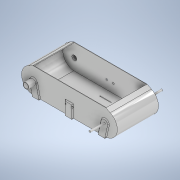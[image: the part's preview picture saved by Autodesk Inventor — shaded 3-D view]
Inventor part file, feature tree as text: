
AUTODESK INVENTOR PART (.ipt)
format: ipt  version: 2021 (Build 250183000, 183)  size: 548,352 bytes
history: native  units: mm
features: sketch x20, extrude x19, projected_geometry x8, fillet x3
ambient origin geometry x8: Origin, YZ Plane, XZ Plane, XY Plane, X Axis, Y Axis, Z Axis, Center Point
bodies: Solid1 (feature_tree)
feature tree (50):
  extrude  "Extrusion1"  Depth=26.0mm
  extrude  "Extrusion3"  Depth=8.0mm
  extrude  "Extrusion4"  Depth=182.8mm TaperAngle=0.0deg
  extrude  "Extrusion5"  Depth=35.0mm TaperAngle=0.0deg
  extrude  "Extrusion6"  Depth=10.0mm TaperAngle=0.0deg
  extrude  "Extrusion7"  Depth=10.0mm
  extrude  "Extrusion8"  Depth=10.0mm
  extrude  "Extrusion12"  Depth=3.0mm
  sketch  "Sketch15"  dims[d42=10.0mm d44=2.0mm]
  extrude  "Extrusion13"  Depth=3.0mm
  sketch  "Sketch17"  dims[d48=4.712389mm d49=3.0mm]
  extrude  "Extrusion14"  Depth=40.0mm
  extrude  "wzmocnienie ramy 1"  Depth=10.0mm
  extrude  "wzmocnienie ramy 2"  Depth=160.0mm
  extrude  "wzmocnienie ramy 3"  TaperAngle=0.0deg  [1 undecoded]
  fillet  "spaw 1"  Radius=10.0mm
  extrude  "wzmocnienie ramy 4"  Depth=4.0mm TaperAngle=0.0deg
  extrude  "wzmocnienie 5"  Depth=4.0mm TaperAngle=0.0deg
  extrude  "wzmocnienie ramy 6"  Depth=4.0mm
  fillet  "spaw 2"  Radius=4.0mm
  extrude  "wzmocnienie ramy 7"  Depth=4.0mm TaperAngle=0.0deg
  extrude  "wzmocnienie ramy 8"  Depth=4.0mm TaperAngle=0.0deg
  extrude  "wzmocnienie ramy 9"  Depth=3.9mm
  fillet  "spaw 3"  Radius=30.0mm
  sketch  "Sketch28"  dims[d85=4.0mm d86=0.0mm d87=3.9mm d88=30.0mm d89=4.0mm d90=4.0mm d91=4.0mm d92=0.0mm d93=30.0mm d94=4.0mm d95=0.0mm d96=4.0mm d97=0.0mm d98=3.9mm]
  sketch  "Sketch1"  dims[d0=22.0mm d1=26.0mm]
  sketch  "Sketch3"  dims[d2=35.0mm d3=0.0mm]
  sketch  "Sketch6"  dims[d14=80.0mm d15=45.0mm d16=135.0deg d17=162.5mm d18=135.0deg d19=50.0mm d20=2.0mm d21=0.0mm d22=8.0mm]
  projected_geometry  "Projected Loop1"
  sketch  "Sketch7"  dims[d23=70.0mm d24=0.0mm d26=182.8mm d27=0.0mm]
  projected_geometry  "Projected Loop2"
  projected_geometry  "Projected Loop3"
  sketch  "Sketch8"  dims[d28=2.0mm d29=0.0mm d30=35.0mm d31=0.0mm]
  sketch  "Sketch9"  dims[d32=70.0mm d33=0.0mm d40=10.0mm d41=0.0mm]
  projected_geometry  "Projected Loop5"
  projected_geometry  "Projected Loop6"
  projected_geometry  "Projected Loop7"
  projected_geometry  "Projected Loop8"
  projected_geometry  "Projected Loop9"
  sketch  "Sketch16"  dims[d45=10.0mm d46=0.0mm d47=26.703538mm]
  sketch  "Sketch18"  dims[d50=3.0mm d51=3.0mm]
  sketch  "Sketch19"  dims[d52=50.0mm d53=40.0mm]
  sketch  "Sketch20"  dims[d54=40.0mm d55=20.0mm d57=102.8mm d58=10.0mm d60=10.0mm]
  sketch  "Sketch21"  dims[d62=0.0mm d63=0.0mm d64=160.0mm]
  sketch  "Sketch22"  dims[d65=30.0mm d66=0.0mm d67=10.0mm]
  sketch  "Sketch23"  dims[d68=54.0mm d69=4.0mm d70=0.0mm]
  sketch  "Sketch24"  dims[d71=4.0mm d72=0.0mm d73=4.0mm d74=0.0mm]
  sketch  "Sketch25"  dims[d75=4.0mm d76=30.0mm d77=4.0mm]
  sketch  "Sketch26"  dims[d79=4.0mm d80=4.0mm d81=0.0mm]
  sketch  "Sketch27"  dims[d82=30.0mm d83=4.0mm d84=0.0mm]
note: 1 required parameter value undecoded (feature->parameter linkage not recoverable at this tier; creation-order binding heuristic only, values carry confidence <= 0.55)
